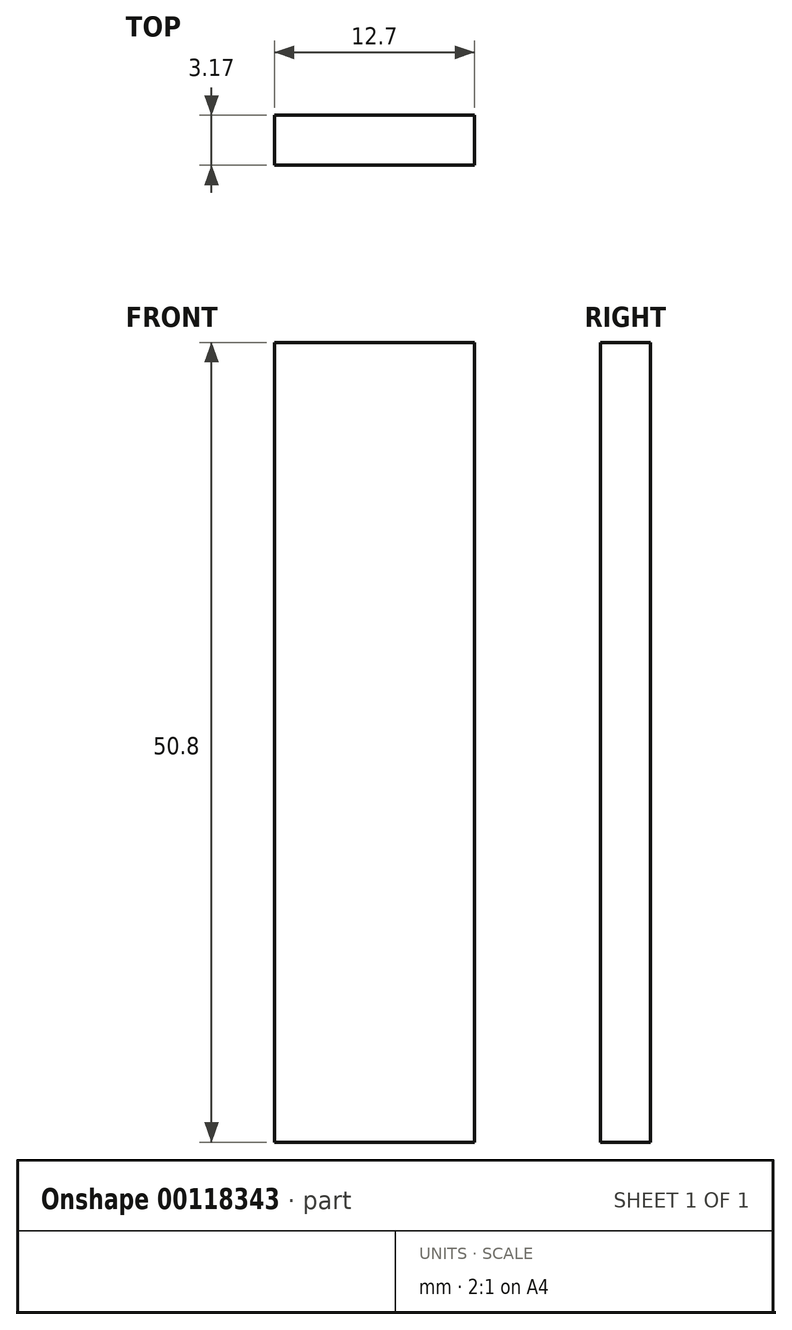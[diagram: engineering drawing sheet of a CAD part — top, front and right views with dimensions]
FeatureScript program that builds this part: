
annotation { "Feature Type Name" : "Feature", "Feature Type Description" : "" }
export const myFeature = defineFeature(function(context is Context, id is Id, definition is map)
    precondition{}
    {
        {
            var Q0;
            Q0=qCreatedBy(makeId("Front.planeOp"),FACE);
            var sketch = newSketch(context, id + "F0", { "sketchPlane" : qUnion([Q0])});
            skLineSegment(sketch, "E0.bottom", {"start": v(6.35, 25.4) * mm, "end": v(-6.35, 25.4) * mm});
            skLineSegment(sketch, "E0.top", {"start": v(6.35, -25.4) * mm, "end": v(-6.35, -25.4) * mm});
            skLineSegment(sketch, "E0.left", {"start": v(6.35, 25.4) * mm, "end": v(6.35, -25.4) * mm});
            skLineSegment(sketch, "E0.right", {"start": v(-6.35, 25.4) * mm, "end": v(-6.35, -25.4) * mm});
            skPoint(sketch, "E0.middle", {"position": v(0, 0) * mm});
            skSolve(sketch);
        }
        {
            var Q0;
            Q0 = qSketchRegion(id + "F0", true);
            extrude(context, id + "F1", {"entities" : qUnion([Q0]), "depth" : 3.17 * mm});
        }
    });
